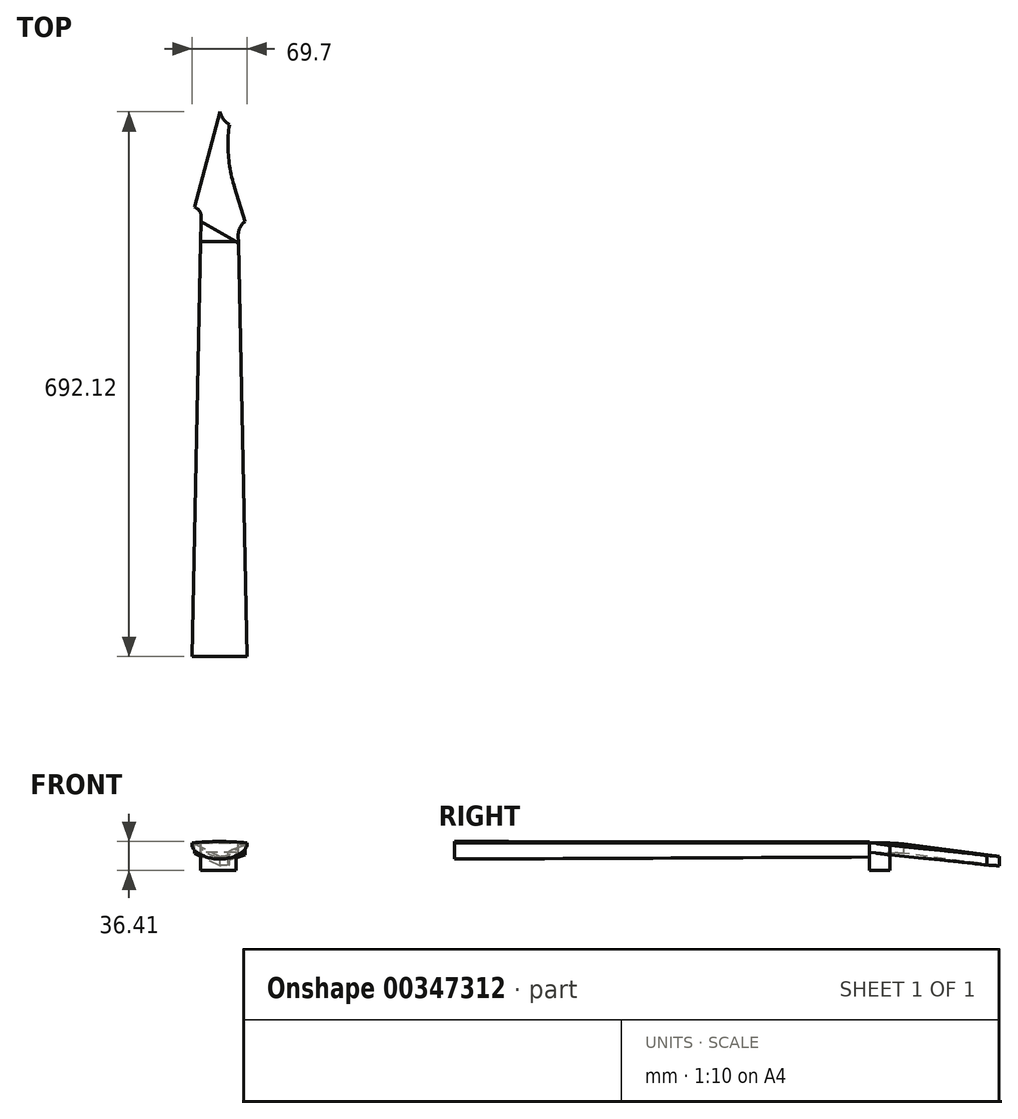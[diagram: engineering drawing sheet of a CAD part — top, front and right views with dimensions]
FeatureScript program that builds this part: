
annotation { "Feature Type Name" : "Feature", "Feature Type Description" : "" }
export const myFeature = defineFeature(function(context is Context, id is Id, definition is map)
    precondition{}
    {
        {
            var Q0;
            Q0=qCreatedBy(makeId("Top.planeOp"),FACE);
            var sketch = newSketch(context, id + "F0", { "sketchPlane" : qUnion([Q0])});
            skLineSegment(sketch, "E0", {"start": v(-24, 485.77) * mm, "end": v(24, 485.77) * mm, "construction": true});
            skLineSegment(sketch, "E1", {"start": v(-50, -161.93) * mm, "end": v(50, -161.93) * mm, "construction": true});
            skLineSegment(sketch, "E2", {"start": v(0, 485.77) * mm, "end": v(0, -161.93) * mm, "construction": true});
            skLineSegment(sketch, "E3", {"start": v(-34, 0) * mm, "end": v(34, 0) * mm, "construction": true});
            skPoint(sketch, "E4", {"position": v(0, 0) * mm});
            skPoint(sketch, "E5", {"position": v(21, 485.77) * mm});
            skSolve(sketch);
        }
        {
            var Q0;
            Q0=qCreatedBy(makeId("Top.planeOp"),FACE);
            var sketch = newSketch(context, id + "F1", { "sketchPlane" : qUnion([Q0])});
            skLineSegment(sketch, "E6", {"start": v(24, 485.77) * mm, "end": v(21, 485.77) * mm, "construction": true});
            skLineSegment(sketch, "E7", {"start": v(21, 485.77) * mm, "end": v(20.77, 485.77) * mm});
            skLineSegment(sketch, "E8", {"start": v(20.77, 485.77) * mm, "end": v(14.57, 485.77) * mm, "construction": true});
            skLineSegment(sketch, "E9", {"start": v(14.57, 485.77) * mm, "end": v(14.29, 485.77) * mm});
            skLineSegment(sketch, "E10", {"start": v(14.29, 485.77) * mm, "end": v(8.08, 485.77) * mm, "construction": true});
            skLineSegment(sketch, "E11", {"start": v(8.08, 485.77) * mm, "end": v(7.68, 485.77) * mm});
            skLineSegment(sketch, "E12", {"start": v(7.68, 485.77) * mm, "end": v(1.47, 485.77) * mm, "construction": true});
            skLineSegment(sketch, "E13", {"start": v(1.47, 485.77) * mm, "end": v(0.86, 485.77) * mm});
            skLineSegment(sketch, "E14", {"start": v(0.86, 485.77) * mm, "end": v(-5.34, 485.77) * mm, "construction": true});
            skLineSegment(sketch, "E15", {"start": v(-5.34, 485.77) * mm, "end": v(-6.15, 485.77) * mm});
            skLineSegment(sketch, "E16", {"start": v(-6.15, 485.77) * mm, "end": v(-12.36, 485.77) * mm, "construction": true});
            skLineSegment(sketch, "E17", {"start": v(-12.36, 485.77) * mm, "end": v(-13.42, 485.77) * mm});
            skLineSegment(sketch, "E18", {"start": v(-13.42, 485.77) * mm, "end": v(-19.63, 485.77) * mm, "construction": true});
            skLineSegment(sketch, "E19", {"start": v(-19.63, 485.77) * mm, "end": v(-21, 485.77) * mm});
            skLineSegment(sketch, "E20", {"start": v(-21, 485.77) * mm, "end": v(-24, 485.77) * mm, "construction": true});
            skPoint(sketch, "E21", {"position": v(-20.32, 485.77) * mm});
            skPoint(sketch, "E22", {"position": v(-12.9, 485.77) * mm});
            skPoint(sketch, "E23", {"position": v(-5.75, 485.77) * mm});
            skPoint(sketch, "E24", {"position": v(1.17, 485.77) * mm});
            skPoint(sketch, "E25", {"position": v(7.88, 485.77) * mm});
            skPoint(sketch, "E26", {"position": v(14.43, 485.77) * mm});
            skPoint(sketch, "E27", {"position": v(20.89, 485.77) * mm});
            skLineSegment(sketch, "E28", {"start": v(34, 0) * mm, "end": v(30.89, 0) * mm});
            skLineSegment(sketch, "E29", {"start": v(30.89, 0) * mm, "end": v(30.66, 0) * mm});
            skLineSegment(sketch, "E30", {"start": v(30.66, 0) * mm, "end": v(21.16, 0) * mm});
            skLineSegment(sketch, "E31", {"start": v(21.16, 0) * mm, "end": v(20.88, 0) * mm});
            skLineSegment(sketch, "E32", {"start": v(20.88, 0) * mm, "end": v(11.38, 0) * mm});
            skLineSegment(sketch, "E33", {"start": v(11.38, 0) * mm, "end": v(10.97, 0) * mm});
            skLineSegment(sketch, "E34", {"start": v(10.97, 0) * mm, "end": v(1.47, 0) * mm});
            skLineSegment(sketch, "E35", {"start": v(1.47, 0) * mm, "end": v(0.86, 0) * mm});
            skLineSegment(sketch, "E36", {"start": v(0.86, 0) * mm, "end": v(-8.64, 0) * mm});
            skLineSegment(sketch, "E37", {"start": v(-8.64, 0) * mm, "end": v(-9.45, 0) * mm});
            skLineSegment(sketch, "E38", {"start": v(-9.45, 0) * mm, "end": v(-18.95, 0) * mm});
            skLineSegment(sketch, "E39", {"start": v(-18.95, 0) * mm, "end": v(-20.02, 0) * mm});
            skLineSegment(sketch, "E40", {"start": v(-20.02, 0) * mm, "end": v(-29.52, 0) * mm});
            skLineSegment(sketch, "E41", {"start": v(-29.52, 0) * mm, "end": v(-30.89, 0) * mm});
            skLineSegment(sketch, "E42", {"start": v(-30.89, 0) * mm, "end": v(-34, 0) * mm});
            skPoint(sketch, "E43", {"position": v(-30.2, 0) * mm});
            skPoint(sketch, "E44", {"position": v(-19.48, 0) * mm});
            skPoint(sketch, "E45", {"position": v(-9.04, 0) * mm});
            skPoint(sketch, "E46", {"position": v(1.17, 0) * mm});
            skPoint(sketch, "E47", {"position": v(11.18, 0) * mm});
            skPoint(sketch, "E48", {"position": v(21.02, 0) * mm});
            skPoint(sketch, "E49", {"position": v(30.78, 0) * mm});
            skLineSegment(sketch, "E50", {"start": v(37.19, -161.93) * mm, "end": v(34.19, -161.93) * mm, "construction": true});
            skLineSegment(sketch, "E51", {"start": v(34.19, -161.93) * mm, "end": v(33.96, -161.93) * mm});
            skLineSegment(sketch, "E52", {"start": v(33.96, -161.93) * mm, "end": v(23.36, -161.93) * mm, "construction": true});
            skLineSegment(sketch, "E53", {"start": v(23.36, -161.93) * mm, "end": v(23.08, -161.93) * mm});
            skLineSegment(sketch, "E54", {"start": v(23.08, -161.93) * mm, "end": v(12.48, -161.93) * mm, "construction": true});
            skLineSegment(sketch, "E55", {"start": v(12.48, -161.93) * mm, "end": v(12.07, -161.93) * mm});
            skLineSegment(sketch, "E56", {"start": v(12.07, -161.93) * mm, "end": v(1.47, -161.93) * mm, "construction": true});
            skLineSegment(sketch, "E57", {"start": v(1.47, -161.93) * mm, "end": v(0.86, -161.93) * mm});
            skLineSegment(sketch, "E58", {"start": v(0.86, -161.93) * mm, "end": v(-9.74, -161.93) * mm, "construction": true});
            skLineSegment(sketch, "E59", {"start": v(-9.74, -161.93) * mm, "end": v(-10.55, -161.93) * mm});
            skLineSegment(sketch, "E60", {"start": v(-10.55, -161.93) * mm, "end": v(-21.15, -161.93) * mm, "construction": true});
            skLineSegment(sketch, "E61", {"start": v(-21.15, -161.93) * mm, "end": v(-22.21, -161.93) * mm});
            skLineSegment(sketch, "E62", {"start": v(-22.21, -161.93) * mm, "end": v(-32.81, -161.93) * mm, "construction": true});
            skLineSegment(sketch, "E63", {"start": v(-32.81, -161.93) * mm, "end": v(-34.19, -161.93) * mm});
            skLineSegment(sketch, "E64", {"start": v(-34.19, -161.93) * mm, "end": v(-37.19, -161.93) * mm, "construction": true});
            skPoint(sketch, "E65", {"position": v(-33.5, -161.93) * mm});
            skPoint(sketch, "E66", {"position": v(-21.68, -161.93) * mm});
            skPoint(sketch, "E67", {"position": v(-10.14, -161.93) * mm});
            skPoint(sketch, "E68", {"position": v(1.17, -161.93) * mm});
            skPoint(sketch, "E69", {"position": v(12.28, -161.93) * mm});
            skPoint(sketch, "E70", {"position": v(23.22, -161.93) * mm});
            skPoint(sketch, "E71", {"position": v(34.07, -161.93) * mm});
            skLineSegment(sketch, "E72", {"start": v(-37.19, -161.93) * mm, "end": v(-37.19, -211.93) * mm, "construction": true});
            skLineSegment(sketch, "E73", {"start": v(-37.19, -211.93) * mm, "end": v(37.19, -211.93) * mm, "construction": true});
            skLineSegment(sketch, "E74", {"start": v(37.19, -211.93) * mm, "end": v(37.19, -161.93) * mm, "construction": true});
            skPoint(sketch, "E75", {"position": v(0, -211.93) * mm});
            skLineSegment(sketch, "E76", {"start": v(-24, 485.77) * mm, "end": v(-23.38, 515.77) * mm, "construction": true});
            skLineSegment(sketch, "E77", {"start": v(-23.38, 515.77) * mm, "end": v(23.38, 515.77) * mm, "construction": true});
            skLineSegment(sketch, "E78", {"start": v(23.38, 515.77) * mm, "end": v(24, 485.77) * mm, "construction": true});
            skLineSegment(sketch, "E79", {"start": v(24, 485.77) * mm, "end": v(38.36, -211.93) * mm});
            skLineSegment(sketch, "E80", {"start": v(-24, 485.78) * mm, "end": v(-38.36, -211.93) * mm});
            skSolve(sketch);
        }
        {
            var Q0;
            Q0=qCreatedBy(makeId("Top.planeOp"),FACE);
            var sketch = newSketch(context, id + "F2", { "sketchPlane" : qUnion([Q0])});
            skLineSegment(sketch, "E81", {"start": v(17.82, 636.3) * mm, "end": v(34.14, -165.06) * mm});
            skLineSegment(sketch, "E82", {"start": v(-17.25, 636.37) * mm, "end": v(-34.31, -201.78) * mm});
            skSolve(sketch);
        }
        {
            var Q0;
            Q0=qCreatedBy(makeId("Top.planeOp"),FACE);
            var sketch = newSketch(context, id + "F3", { "sketchPlane" : qUnion([Q0])});
            skLineSegment(sketch, "E83", {"start": v(23.32, -169.15) * mm, "end": v(12.4, 634.88) * mm});
            skLineSegment(sketch, "E84", {"start": v(-10.88, 634.32) * mm, "end": v(-22.08, -191.54) * mm});
            skLineSegment(sketch, "E85", {"start": v(12.36, -173.72) * mm, "end": v(6.89, 632.04) * mm});
            skLineSegment(sketch, "E86", {"start": v(-10.3, -185.7) * mm, "end": v(-4.74, 634.55) * mm});
            skLineSegment(sketch, "E87", {"start": v(1.17, 632.04) * mm, "end": v(1.17, -180.14) * mm});
            skSolve(sketch);
        }
        {
            var Q0;
            Q0=qCreatedBy(makeId("Top.planeOp"),FACE);
            var sketch = newSketch(context, id + "F4", { "sketchPlane" : qUnion([Q0])});
            skLineSegment(sketch, "E88", {"start": v(0, 515.7) * mm, "end": v(0, -207.7) * mm});
            skLineSegment(sketch, "E89", {"start": v(-52.5, 223.2) * mm, "end": v(52.5, 223.2) * mm});
            skPoint(sketch, "E90", {"position": v(0, 223.2) * mm});
            skLineSegment(sketch, "E91", {"start": v(0, 246.1) * mm, "end": v(52.5, 246.1) * mm});
            skLineSegment(sketch, "E92", {"start": v(52.5, 270.36) * mm, "end": v(0, 270.36) * mm});
            skLineSegment(sketch, "E93", {"start": v(0, 323.3) * mm, "end": v(52.5, 323.3) * mm});
            skLineSegment(sketch, "E94", {"start": v(52.5, 352.15) * mm, "end": v(0, 352.15) * mm});
            skLineSegment(sketch, "E95", {"start": v(0, 382.72) * mm, "end": v(52.5, 382.72) * mm});
            skLineSegment(sketch, "E96", {"start": v(52.5, 415.1) * mm, "end": v(0, 415.1) * mm});
            skLineSegment(sketch, "E97", {"start": v(0, 449.42) * mm, "end": v(52.5, 449.42) * mm});
            skLineSegment(sketch, "E98", {"start": v(52.5, 485.77) * mm, "end": v(0, 485.77) * mm});
            skLineSegment(sketch, "E99", {"start": v(0, 432.42) * mm, "end": v(-52.5, 432.42) * mm});
            skLineSegment(sketch, "E100", {"start": v(0, 397.11) * mm, "end": v(-52.5, 397.11) * mm});
            skLineSegment(sketch, "E101", {"start": v(-52.5, 363.79) * mm, "end": v(0, 363.79) * mm});
            skLineSegment(sketch, "E102", {"start": v(0, 469.83) * mm, "end": v(-52.5, 469.83) * mm});
            skLineSegment(sketch, "E103", {"start": v(-52.5, 332.33) * mm, "end": v(0, 332.33) * mm});
            skLineSegment(sketch, "E104", {"start": v(0, 302.64) * mm, "end": v(-52.5, 302.64) * mm});
            skLineSegment(sketch, "E105", {"start": v(-52.5, 274.62) * mm, "end": v(0, 274.62) * mm});
            skLineSegment(sketch, "E106", {"start": v(0, 80.69) * mm, "end": v(52.5, 80.69) * mm});
            skLineSegment(sketch, "E107", {"start": v(52.5, 95.12) * mm, "end": v(0, 95.12) * mm});
            skLineSegment(sketch, "E108", {"start": v(0, 110.4) * mm, "end": v(52.5, 110.4) * mm});
            skLineSegment(sketch, "E109", {"start": v(52.5, 126.6) * mm, "end": v(0, 126.6) * mm});
            skLineSegment(sketch, "E110", {"start": v(0, 143.75) * mm, "end": v(52.5, 143.75) * mm});
            skLineSegment(sketch, "E111", {"start": v(52.5, 161.93) * mm, "end": v(0, 161.93) * mm});
            skLineSegment(sketch, "E112", {"start": v(0, 181.18) * mm, "end": v(52.5, 181.18) * mm});
            skLineSegment(sketch, "E113", {"start": v(52.5, 201.58) * mm, "end": v(0, 201.58) * mm});
            skLineSegment(sketch, "E114", {"start": v(-52.5, 83.56) * mm, "end": v(0, 83.56) * mm});
            skLineSegment(sketch, "E115", {"start": v(0, 100.22) * mm, "end": v(-52.5, 100.22) * mm});
            skLineSegment(sketch, "E116", {"start": v(-52.5, 117.88) * mm, "end": v(0, 117.88) * mm});
            skLineSegment(sketch, "E117", {"start": v(0, 136.58) * mm, "end": v(-52.5, 136.58) * mm});
            skLineSegment(sketch, "E118", {"start": v(-52.5, 156.4) * mm, "end": v(0, 156.4) * mm});
            skLineSegment(sketch, "E119", {"start": v(0, 177.4) * mm, "end": v(-52.5, 177.4) * mm});
            skLineSegment(sketch, "E120", {"start": v(-52.5, 199.63) * mm, "end": v(0, 199.63) * mm});
            skLineSegment(sketch, "E121", {"start": v(0, 248.17) * mm, "end": v(-52.5, 248.17) * mm});
            skLineSegment(sketch, "E122", {"start": v(0, 296.07) * mm, "end": v(52.5, 296.07) * mm});
            skLineSegment(sketch, "E123", {"start": v(0, 0) * mm, "end": v(52.5, 0) * mm});
            skLineSegment(sketch, "E124", {"start": v(52.5, 9.63) * mm, "end": v(0, 9.63) * mm});
            skLineSegment(sketch, "E125", {"start": v(0, 19.83) * mm, "end": v(52.5, 19.83) * mm});
            skLineSegment(sketch, "E126", {"start": v(52.5, 30.64) * mm, "end": v(0, 30.64) * mm});
            skLineSegment(sketch, "E127", {"start": v(0, 42.09) * mm, "end": v(52.5, 42.09) * mm});
            skLineSegment(sketch, "E128", {"start": v(52.5, 54.22) * mm, "end": v(0, 54.22) * mm});
            skLineSegment(sketch, "E129", {"start": v(0, 67.07) * mm, "end": v(52.5, 67.07) * mm});
            skLineSegment(sketch, "E130", {"start": v(0, -161.93) * mm, "end": v(52.5, -161.93) * mm});
            skLineSegment(sketch, "E131", {"start": v(0, -196.66) * mm, "end": v(-52.5, -196.66) * mm});
            skLineSegment(sketch, "E132", {"start": v(0, 509.46) * mm, "end": v(-60, 509.46) * mm});
            skLineSegment(sketch, "E133", {"start": v(-52.5, -9.64) * mm, "end": v(0, -9.64) * mm});
            skLineSegment(sketch, "E134", {"start": v(0, 1.49) * mm, "end": v(-52.5, 1.49) * mm});
            skLineSegment(sketch, "E135", {"start": v(-52.5, 13.27) * mm, "end": v(0, 13.27) * mm});
            skLineSegment(sketch, "E136", {"start": v(0, 25.75) * mm, "end": v(-52.5, 25.75) * mm});
            skLineSegment(sketch, "E137", {"start": v(-52.5, 38.98) * mm, "end": v(0, 38.98) * mm});
            skLineSegment(sketch, "E138", {"start": v(0, 52.99) * mm, "end": v(-52.5, 52.99) * mm});
            skLineSegment(sketch, "E139", {"start": v(-52.5, 67.83) * mm, "end": v(0, 67.83) * mm});
            skLineSegment(sketch, "E140", {"start": v(0, -20.13) * mm, "end": v(-52.5, -20.13) * mm});
            skSolve(sketch);
        }
        {
            var Q0;
            Q0=qCreatedBy(makeId("Top.planeOp"),FACE);
            var sketch = newSketch(context, id + "F5", { "sketchPlane" : qUnion([Q0])});
            skLineSegment(sketch, "E141", {"start": v(24.04, 483.94) * mm, "end": v(-23.47, 511.57) * mm});
            skPoint(sketch, "E142", {"position": v(-19.83, 509.46) * mm});
            skLineSegment(sketch, "E143", {"start": v(-24.3, 471.6) * mm, "end": v(24.78, 447.9) * mm});
            skLineSegment(sketch, "E144", {"start": v(-25.07, 433.87) * mm, "end": v(25.48, 413.86) * mm});
            skLineSegment(sketch, "E145", {"start": v(-25.8, 398.29) * mm, "end": v(26.14, 381.72) * mm});
            skLineSegment(sketch, "E146", {"start": v(-26.5, 364.71) * mm, "end": v(26.77, 351.36) * mm});
            skLineSegment(sketch, "E147", {"start": v(-27.14, 333.03) * mm, "end": v(27.36, 322.7) * mm});
            skLineSegment(sketch, "E148", {"start": v(-27.76, 303.14) * mm, "end": v(27.91, 295.64) * mm});
            skLineSegment(sketch, "E149", {"start": v(-28.34, 274.93) * mm, "end": v(28.44, 270.1) * mm});
            skLineSegment(sketch, "E150", {"start": v(-28.89, 248.32) * mm, "end": v(28.94, 245.97) * mm});
            skLineSegment(sketch, "E151", {"start": v(-29.4, 223.2) * mm, "end": v(29.4, 223.2) * mm});
            skLineSegment(sketch, "E152", {"start": v(29.85, 201.7) * mm, "end": v(-29.9, 199.5) * mm});
            skLineSegment(sketch, "E153", {"start": v(30.27, 181.4) * mm, "end": v(-30.35, 177.13) * mm});
            skLineSegment(sketch, "E154", {"start": v(30.66, 162.25) * mm, "end": v(-30.79, 156.02) * mm});
            skLineSegment(sketch, "E155", {"start": v(31.03, 144.16) * mm, "end": v(-31.2, 136.1) * mm});
            skLineSegment(sketch, "E156", {"start": v(31.38, 127.09) * mm, "end": v(-31.59, 117.3) * mm});
            skLineSegment(sketch, "E157", {"start": v(32.03, 95.76) * mm, "end": v(-32.3, 82.8) * mm});
            skLineSegment(sketch, "E158", {"start": v(32.32, 81.4) * mm, "end": v(-32.62, 67) * mm});
            skLineSegment(sketch, "E159", {"start": v(32.6, 67.84) * mm, "end": v(-32.93, 52.07) * mm});
            skLineSegment(sketch, "E160", {"start": v(32.87, 55.04) * mm, "end": v(-33.22, 38) * mm});
            skLineSegment(sketch, "E161", {"start": v(33.12, 42.97) * mm, "end": v(-33.5, 24.7) * mm});
            skLineSegment(sketch, "E162", {"start": v(33.35, 31.56) * mm, "end": v(-33.75, 12.17) * mm});
            skLineSegment(sketch, "E163", {"start": v(33.57, 20.8) * mm, "end": v(-34, 0.33) * mm});
            skLineSegment(sketch, "E164", {"start": v(33.78, 10.64) * mm, "end": v(-34.22, -10.84) * mm});
            skLineSegment(sketch, "E165", {"start": v(33.98, 1.05) * mm, "end": v(-34.44, -21.39) * mm});
            skPoint(sketch, "E166", {"position": v(-30.61, -20.13) * mm});
            skPoint(sketch, "E167", {"position": v(-30.4, -9.64) * mm});
            skPoint(sketch, "E168", {"position": v(-30.17, 1.49) * mm});
            skPoint(sketch, "E169", {"position": v(-29.93, 13.27) * mm});
            skPoint(sketch, "E170", {"position": v(-29.68, 25.75) * mm});
            skPoint(sketch, "E171", {"position": v(-29.41, 38.98) * mm});
            skPoint(sketch, "E172", {"position": v(-29.13, 52.99) * mm});
            skPoint(sketch, "E173", {"position": v(-28.82, 67.83) * mm});
            skPoint(sketch, "E174", {"position": v(-28.5, 83.56) * mm});
            skPoint(sketch, "E175", {"position": v(-28.16, 100.22) * mm});
            skPoint(sketch, "E176", {"position": v(-27.8, 117.88) * mm});
            skPoint(sketch, "E177", {"position": v(-27.42, 136.58) * mm});
            skPoint(sketch, "E178", {"position": v(-27.02, 156.4) * mm});
            skPoint(sketch, "E179", {"position": v(-26.6, 177.4) * mm});
            skPoint(sketch, "E180", {"position": v(-26.14, 199.63) * mm});
            skPoint(sketch, "E181", {"position": v(-25.66, 223.2) * mm});
            skPoint(sketch, "E182", {"position": v(-25.15, 248.17) * mm});
            skPoint(sketch, "E183", {"position": v(-24.61, 274.62) * mm});
            skPoint(sketch, "E184", {"position": v(-24.04, 302.64) * mm});
            skPoint(sketch, "E185", {"position": v(-23.44, 332.33) * mm});
            skPoint(sketch, "E186", {"position": v(-22.8, 363.79) * mm});
            skPoint(sketch, "E187", {"position": v(-22.12, 397.11) * mm});
            skPoint(sketch, "E188", {"position": v(-21.4, 432.42) * mm});
            skPoint(sketch, "E189", {"position": v(-20.64, 469.83) * mm});
            skLineSegment(sketch, "E190", {"start": v(-31.95, 99.55) * mm, "end": v(31.72, 110.97) * mm});
            skPoint(sketch, "E191", {"position": v(30.58, 9.63) * mm});
            skPoint(sketch, "E192", {"position": v(30.37, 19.83) * mm});
            skPoint(sketch, "E193", {"position": v(30.15, 30.64) * mm});
            skPoint(sketch, "E194", {"position": v(29.92, 42.09) * mm});
            skPoint(sketch, "E195", {"position": v(29.67, 54.22) * mm});
            skPoint(sketch, "E196", {"position": v(29.4, 67.07) * mm});
            skPoint(sketch, "E197", {"position": v(29.13, 80.69) * mm});
            skPoint(sketch, "E198", {"position": v(28.84, 95.12) * mm});
            skPoint(sketch, "E199", {"position": v(28.53, 110.4) * mm});
            skPoint(sketch, "E200", {"position": v(28.2, 126.6) * mm});
            skPoint(sketch, "E201", {"position": v(27.85, 143.75) * mm});
            skPoint(sketch, "E202", {"position": v(27.48, 161.93) * mm});
            skPoint(sketch, "E203", {"position": v(27.09, 181.18) * mm});
            skPoint(sketch, "E204", {"position": v(26.67, 201.58) * mm});
            skPoint(sketch, "E205", {"position": v(26.23, 223.2) * mm});
            skPoint(sketch, "E206", {"position": v(25.77, 246.1) * mm});
            skPoint(sketch, "E207", {"position": v(25.27, 270.36) * mm});
            skPoint(sketch, "E208", {"position": v(24.75, 296.07) * mm});
            skPoint(sketch, "E209", {"position": v(24.2, 323.3) * mm});
            skPoint(sketch, "E210", {"position": v(23.6, 352.15) * mm});
            skPoint(sketch, "E211", {"position": v(22.98, 382.72) * mm});
            skPoint(sketch, "E212", {"position": v(22.33, 415.1) * mm});
            skPoint(sketch, "E213", {"position": v(21.63, 449.42) * mm});
            skLineSegment(sketch, "E214", {"start": v(34.07, -161.92) * mm, "end": v(-34.2, -196.66) * mm});
            skSolve(sketch);
        }
        {
            var Q0;
            Q0=qCreatedBy(makeId("Top.planeOp"),FACE);
            var sketch = newSketch(context, id + "F6", { "sketchPlane" : qUnion([Q0])});
            skCircle(sketch, "E215", {"center": v(-28.12, 544.63) * mm, "radius": 3 * mm});
            skCircle(sketch, "E216", {"center": v(20.37, 536.39) * mm, "radius": 3 * mm});
            skCircle(sketch, "E217", {"center": v(28.47, 515.94) * mm, "radius": 3 * mm});
            skLineSegment(sketch, "E218", {"start": v(-28.12, 544.63) * mm, "end": v(-19.36, 564.81) * mm, "construction": true});
            skCircle(sketch, "E219", {"center": v(-28.12, 544.63) * mm, "radius": 8.15 * mm, "construction": true});
            skCircle(sketch, "E220", {"center": v(-19.36, 564.81) * mm, "radius": 8.15 * mm, "construction": true});
            skCircle(sketch, "E221", {"center": v(-10.6, 585) * mm, "radius": 8.15 * mm, "construction": true});
            skCircle(sketch, "E222", {"center": v(28.47, 515.94) * mm, "radius": 8.15 * mm, "construction": true});
            skLineSegment(sketch, "E223", {"start": v(-23.47, 511.57) * mm, "end": v(-25.07, 433.87) * mm});
            skLineSegment(sketch, "E224", {"start": v(24.04, 483.94) * mm, "end": v(25.48, 413.86) * mm});
            skLineSegment(sketch, "E225", {"start": v(-19.36, 564.81) * mm, "end": v(-10.6, 585) * mm, "construction": true});
            skCircle(sketch, "E226", {"center": v(-1.83, 605.17) * mm, "radius": 3 * mm});
            skCircle(sketch, "E227", {"center": v(-1.83, 605.17) * mm, "radius": 8.15 * mm, "construction": true});
            skLineSegment(sketch, "E228", {"start": v(-10.6, 585) * mm, "end": v(-1.83, 605.17) * mm, "construction": true});
            skLineSegment(sketch, "E229", {"start": v(12.27, 556.84) * mm, "end": v(20.37, 536.39) * mm, "construction": true});
            skLineSegment(sketch, "E230", {"start": v(20.37, 536.39) * mm, "end": v(28.47, 515.94) * mm, "construction": true});
            skLineSegment(sketch, "E231", {"start": v(-38.84, 540.4) * mm, "end": v(6.93, 645.82) * mm});
            skCircle(sketch, "E232", {"center": v(6.93, 625.35) * mm, "radius": 3 * mm});
            skCircle(sketch, "E233", {"center": v(6.93, 625.35) * mm, "radius": 8.15 * mm, "construction": true});
            skLineSegment(sketch, "E234", {"start": v(6.93, 625.35) * mm, "end": v(-1.83, 605.17) * mm, "construction": true});
            skLineSegment(sketch, "E235", {"start": v(12.27, 556.84) * mm, "end": v(4.17, 577.3) * mm, "construction": true});
            skCircle(sketch, "E236", {"center": v(4.17, 577.3) * mm, "radius": 3 * mm, "construction": true});
            skLineSegment(sketch, "E237", {"start": v(-28.12, 544.63) * mm, "end": v(-19.12, 544.45) * mm, "construction": true});
            skLineSegment(sketch, "E238", {"start": v(28.47, 515.94) * mm, "end": v(20.28, 515.77) * mm, "construction": true});
            skPoint(sketch, "E239", {"position": v(20.89, 485.77) * mm});
            skLineSegment(sketch, "E240", {"start": v(35.32, 520.36) * mm, "end": v(39.74, 513.52) * mm});
            skLineSegment(sketch, "E241", {"start": v(39.74, 513.52) * mm, "end": v(32.9, 509.1) * mm, "construction": true});
            skArc(sketch, "E242", {"start": v(24.04, 483.94) * mm, "mid": v(28.05, 500.77) * mm, "end": v(39.74, 513.52) * mm});
            skLineSegment(sketch, "E243", {"start": v(-38.84, 540.4) * mm, "end": v(-31.36, 537.16) * mm, "construction": true});
            skLineSegment(sketch, "E244", {"start": v(-23.47, 511.57) * mm, "end": v(-23.37, 516.29) * mm});
            skArc(sketch, "E245", {"start": v(-23.37, 516.29) * mm, "mid": v(-27.44, 530.7) * mm, "end": v(-38.84, 540.4) * mm});
            skArc(sketch, "E246", {"start": v(6.93, 645.82) * mm, "mid": v(9.7, 635.66) * mm, "end": v(16.41, 627.54) * mm});
            skArc(sketch, "E247", {"start": v(35.32, 520.36) * mm, "mid": v(15.02, 572.04) * mm, "end": v(16.41, 627.54) * mm});
            skCircle(sketch, "E248", {"center": v(-10.6, 585) * mm, "radius": 3 * mm});
            skCircle(sketch, "E249", {"center": v(-19.36, 564.81) * mm, "radius": 3 * mm});
            skLineSegment(sketch, "E250", {"start": v(6.93, 625.35) * mm, "end": v(-0.55, 628.6) * mm, "construction": true});
            skSolve(sketch);
        }
        {
            var Q0;
            Q0=qCreatedBy(makeId("Top.planeOp"),FACE);
            var sketch = newSketch(context, id + "F7", { "sketchPlane" : qUnion([Q0])});
            skCircle(sketch, "E251", {"center": v(-22.34, 533.57) * mm, "radius": 3 * mm});
            skCircle(sketch, "E252", {"center": v(-22.34, 533.57) * mm, "radius": 8.15 * mm, "construction": true});
            skCircle(sketch, "E253", {"center": v(-14.87, 561.3) * mm, "radius": 3 * mm});
            skCircle(sketch, "E254", {"center": v(-14.87, 561.3) * mm, "radius": 8.15 * mm, "construction": true});
            skCircle(sketch, "E255", {"center": v(-8.06, 586.53) * mm, "radius": 3 * mm});
            skCircle(sketch, "E256", {"center": v(-8.06, 586.53) * mm, "radius": 8.15 * mm, "construction": true});
            skCircle(sketch, "E257", {"center": v(-1.83, 609.64) * mm, "radius": 3 * mm});
            skCircle(sketch, "E258", {"center": v(-1.83, 609.64) * mm, "radius": 8.15 * mm, "construction": true});
            skCircle(sketch, "E259", {"center": v(3.9, 630.88) * mm, "radius": 3 * mm});
            skCircle(sketch, "E260", {"center": v(3.9, 630.88) * mm, "radius": 8.15 * mm, "construction": true});
            skLineSegment(sketch, "E261", {"start": v(3.9, 630.88) * mm, "end": v(-1.83, 609.64) * mm, "construction": true});
            skLineSegment(sketch, "E262", {"start": v(-1.83, 609.64) * mm, "end": v(-8.06, 586.53) * mm, "construction": true});
            skLineSegment(sketch, "E263", {"start": v(-8.06, 586.53) * mm, "end": v(-14.87, 561.3) * mm, "construction": true});
            skLineSegment(sketch, "E264", {"start": v(-14.87, 561.3) * mm, "end": v(-22.34, 533.57) * mm, "construction": true});
            skCircle(sketch, "E265", {"center": v(23.31, 514.04) * mm, "radius": 3 * mm});
            skCircle(sketch, "E266", {"center": v(23.31, 514.04) * mm, "radius": 8.15 * mm, "construction": true});
            skCircle(sketch, "E267", {"center": v(16.76, 535.04) * mm, "radius": 3 * mm});
            skCircle(sketch, "E268", {"center": v(16.76, 535.04) * mm, "radius": 8.15 * mm, "construction": true});
            skLineSegment(sketch, "E269", {"start": v(16.76, 535.04) * mm, "end": v(23.31, 514.04) * mm, "construction": true});
            skLineSegment(sketch, "E270", {"start": v(-25.07, 433.87) * mm, "end": v(-23.47, 511.57) * mm});
            skLineSegment(sketch, "E271", {"start": v(25.48, 413.86) * mm, "end": v(24.04, 483.94) * mm});
            skLineSegment(sketch, "E272", {"start": v(-31.86, 529.57) * mm, "end": v(0.84, 650.86) * mm});
            skLineSegment(sketch, "E273", {"start": v(-23.47, 511.57) * mm, "end": v(-23.34, 518.07) * mm});
            skArc(sketch, "E274", {"start": v(-23.34, 518.07) * mm, "mid": v(-25.63, 525.28) * mm, "end": v(-31.86, 529.57) * mm});
            skLineSegment(sketch, "E275", {"start": v(24.04, 483.94) * mm, "end": v(23.83, 493.94) * mm});
            skLineSegment(sketch, "E276", {"start": v(32.65, 511.48) * mm, "end": v(19.25, 554.4) * mm});
            skArc(sketch, "E277", {"start": v(23.83, 493.94) * mm, "mid": v(26.06, 503.8) * mm, "end": v(32.65, 511.48) * mm});
            skArc(sketch, "E278", {"start": v(0.84, 650.86) * mm, "mid": v(5.02, 641.55) * mm, "end": v(12.58, 634.68) * mm});
            skLineSegment(sketch, "E279", {"start": v(-23.47, 511.57) * mm, "end": v(1.17, 511.57) * mm});
            skLineSegment(sketch, "E280", {"start": v(3.9, 630.88) * mm, "end": v(-3.97, 633) * mm, "construction": true});
            skArc(sketch, "E281", {"start": v(12.58, 634.68) * mm, "mid": v(11.5, 594.18) * mm, "end": v(19.25, 554.4) * mm});
            skSolve(sketch);
        }
        {
            var Q0;
            Q0=qCreatedBy(makeId("Top.planeOp"),FACE);
            var sketch = newSketch(context, id + "F8", { "sketchPlane" : qUnion([Q0])});
            skLineSegment(sketch, "E282.0", {"start": v(17.82, 636.3) * mm, "end": v(30.78, 0) * mm});
            skLineSegment(sketch, "E282.1", {"start": v(-17.25, 636.37) * mm, "end": v(-34.31, -201.78) * mm});
            skLineSegment(sketch, "E282.2", {"start": v(-17.25, 636.37) * mm, "end": v(-30.61, -20.13) * mm});
            skLineSegment(sketch, "E283.0", {"start": v(23.32, -169.15) * mm, "end": v(12.4, 634.88) * mm});
            skLineSegment(sketch, "E283.1", {"start": v(-10.88, 634.32) * mm, "end": v(-22.08, -191.54) * mm});
            skLineSegment(sketch, "E283.2", {"start": v(12.36, -173.72) * mm, "end": v(6.89, 632.04) * mm});
            skLineSegment(sketch, "E283.3", {"start": v(-10.3, -185.7) * mm, "end": v(-4.74, 634.55) * mm});
            skLineSegment(sketch, "E283.4", {"start": v(1.17, 632.04) * mm, "end": v(1.17, -180.14) * mm});
            skLineSegment(sketch, "E283.5", {"start": v(-10.3, -185.7) * mm, "end": v(-4.74, 634.55) * mm});
            skLineSegment(sketch, "E284.0", {"start": v(24.04, 483.94) * mm, "end": v(-23.47, 511.57) * mm});
            skPoint(sketch, "E284.1", {"position": v(-19.83, 509.46) * mm});
            skLineSegment(sketch, "E284.2", {"start": v(-24.3, 471.6) * mm, "end": v(24.78, 447.9) * mm});
            skLineSegment(sketch, "E284.3", {"start": v(-25.07, 433.87) * mm, "end": v(25.48, 413.86) * mm});
            skLineSegment(sketch, "E284.4", {"start": v(-25.8, 398.29) * mm, "end": v(26.14, 381.72) * mm});
            skLineSegment(sketch, "E284.5", {"start": v(-26.5, 364.71) * mm, "end": v(26.77, 351.36) * mm});
            skLineSegment(sketch, "E284.6", {"start": v(-27.14, 333.03) * mm, "end": v(27.36, 322.7) * mm});
            skLineSegment(sketch, "E284.7", {"start": v(-27.76, 303.14) * mm, "end": v(27.91, 295.64) * mm});
            skLineSegment(sketch, "E284.8", {"start": v(-28.34, 274.93) * mm, "end": v(28.44, 270.1) * mm});
            skLineSegment(sketch, "E284.9", {"start": v(-28.89, 248.32) * mm, "end": v(28.94, 245.97) * mm});
            skLineSegment(sketch, "E284.10", {"start": v(-29.4, 223.2) * mm, "end": v(29.4, 223.2) * mm});
            skLineSegment(sketch, "E284.11", {"start": v(29.85, 201.7) * mm, "end": v(-29.9, 199.5) * mm});
            skLineSegment(sketch, "E284.12", {"start": v(30.27, 181.4) * mm, "end": v(-30.35, 177.13) * mm});
            skLineSegment(sketch, "E284.13", {"start": v(30.66, 162.25) * mm, "end": v(-30.79, 156.02) * mm});
            skLineSegment(sketch, "E284.14", {"start": v(31.03, 144.16) * mm, "end": v(-31.2, 136.1) * mm});
            skLineSegment(sketch, "E284.15", {"start": v(31.38, 127.09) * mm, "end": v(-31.59, 117.3) * mm});
            skLineSegment(sketch, "E284.16", {"start": v(32.03, 95.76) * mm, "end": v(-32.3, 82.8) * mm});
            skLineSegment(sketch, "E284.17", {"start": v(32.32, 81.4) * mm, "end": v(-32.62, 67) * mm});
            skLineSegment(sketch, "E284.18", {"start": v(32.6, 67.84) * mm, "end": v(-32.93, 52.07) * mm});
            skLineSegment(sketch, "E284.19", {"start": v(32.87, 55.04) * mm, "end": v(-33.22, 38) * mm});
            skLineSegment(sketch, "E284.20", {"start": v(33.12, 42.97) * mm, "end": v(-33.5, 24.7) * mm});
            skLineSegment(sketch, "E284.21", {"start": v(33.35, 31.56) * mm, "end": v(-33.75, 12.17) * mm});
            skLineSegment(sketch, "E284.22", {"start": v(33.57, 20.8) * mm, "end": v(-34, 0.33) * mm});
            skLineSegment(sketch, "E284.23", {"start": v(33.78, 10.64) * mm, "end": v(-34.22, -10.84) * mm});
            skLineSegment(sketch, "E284.24", {"start": v(33.98, 1.05) * mm, "end": v(-34.44, -21.39) * mm});
            skPoint(sketch, "E284.27", {"position": v(-30.17, 1.49) * mm});
            skPoint(sketch, "E284.28", {"position": v(-29.93, 13.27) * mm});
            skPoint(sketch, "E284.29", {"position": v(-29.68, 25.75) * mm});
            skPoint(sketch, "E284.30", {"position": v(-29.41, 38.98) * mm});
            skPoint(sketch, "E284.31", {"position": v(-29.13, 52.99) * mm});
            skPoint(sketch, "E284.32", {"position": v(-28.82, 67.83) * mm});
            skPoint(sketch, "E284.33", {"position": v(-28.5, 83.56) * mm});
            skPoint(sketch, "E284.34", {"position": v(-28.16, 100.22) * mm});
            skPoint(sketch, "E284.35", {"position": v(-27.8, 117.88) * mm});
            skPoint(sketch, "E284.36", {"position": v(-27.42, 136.58) * mm});
            skPoint(sketch, "E284.37", {"position": v(-27.02, 156.4) * mm});
            skPoint(sketch, "E284.38", {"position": v(-26.6, 177.4) * mm});
            skPoint(sketch, "E284.39", {"position": v(-26.14, 199.63) * mm});
            skPoint(sketch, "E284.40", {"position": v(-25.66, 223.2) * mm});
            skPoint(sketch, "E284.41", {"position": v(-25.15, 248.17) * mm});
            skPoint(sketch, "E284.42", {"position": v(-24.61, 274.62) * mm});
            skPoint(sketch, "E284.43", {"position": v(-24.04, 302.64) * mm});
            skPoint(sketch, "E284.44", {"position": v(-23.44, 332.33) * mm});
            skPoint(sketch, "E284.45", {"position": v(-22.8, 363.79) * mm});
            skPoint(sketch, "E284.46", {"position": v(-22.12, 397.11) * mm});
            skPoint(sketch, "E284.47", {"position": v(-21.4, 432.42) * mm});
            skPoint(sketch, "E284.48", {"position": v(-20.64, 469.83) * mm});
            skLineSegment(sketch, "E284.49", {"start": v(-31.95, 99.55) * mm, "end": v(31.72, 110.97) * mm});
            skPoint(sketch, "E284.50", {"position": v(30.58, 9.63) * mm});
            skPoint(sketch, "E284.51", {"position": v(30.37, 19.83) * mm});
            skPoint(sketch, "E284.52", {"position": v(30.15, 30.64) * mm});
            skPoint(sketch, "E284.53", {"position": v(29.92, 42.09) * mm});
            skPoint(sketch, "E284.54", {"position": v(29.67, 54.22) * mm});
            skPoint(sketch, "E284.55", {"position": v(29.4, 67.07) * mm});
            skPoint(sketch, "E284.56", {"position": v(29.13, 80.69) * mm});
            skPoint(sketch, "E284.57", {"position": v(28.84, 95.12) * mm});
            skPoint(sketch, "E284.58", {"position": v(28.53, 110.4) * mm});
            skPoint(sketch, "E284.59", {"position": v(28.2, 126.6) * mm});
            skPoint(sketch, "E284.60", {"position": v(27.85, 143.75) * mm});
            skPoint(sketch, "E284.61", {"position": v(27.48, 161.93) * mm});
            skPoint(sketch, "E284.62", {"position": v(27.09, 181.18) * mm});
            skPoint(sketch, "E284.63", {"position": v(26.67, 201.58) * mm});
            skPoint(sketch, "E284.64", {"position": v(26.23, 223.2) * mm});
            skPoint(sketch, "E284.65", {"position": v(25.77, 246.1) * mm});
            skPoint(sketch, "E284.66", {"position": v(25.27, 270.36) * mm});
            skPoint(sketch, "E284.67", {"position": v(24.75, 296.07) * mm});
            skPoint(sketch, "E284.68", {"position": v(24.2, 323.3) * mm});
            skPoint(sketch, "E284.69", {"position": v(23.6, 352.15) * mm});
            skPoint(sketch, "E284.70", {"position": v(22.98, 382.72) * mm});
            skPoint(sketch, "E284.71", {"position": v(22.33, 415.1) * mm});
            skPoint(sketch, "E284.72", {"position": v(21.63, 449.42) * mm});
            skLineSegment(sketch, "E284.73", {"start": v(34.07, -161.92) * mm, "end": v(-34.2, -196.66) * mm});
            skLineSegment(sketch, "E284.74", {"start": v(33.98, 1.05) * mm, "end": v(-34.44, -21.39) * mm});
            skCircle(sketch, "E285.0", {"center": v(-22.34, 533.57) * mm, "radius": 3 * mm});
            skCircle(sketch, "E285.1", {"center": v(-22.34, 533.57) * mm, "radius": 8.15 * mm});
            skCircle(sketch, "E285.2", {"center": v(-14.87, 561.3) * mm, "radius": 3 * mm});
            skCircle(sketch, "E285.3", {"center": v(-14.87, 561.3) * mm, "radius": 8.15 * mm});
            skCircle(sketch, "E285.4", {"center": v(-8.06, 586.53) * mm, "radius": 3 * mm});
            skCircle(sketch, "E285.5", {"center": v(-8.06, 586.53) * mm, "radius": 8.15 * mm});
            skCircle(sketch, "E285.6", {"center": v(-1.83, 609.64) * mm, "radius": 3 * mm});
            skCircle(sketch, "E285.7", {"center": v(-1.83, 609.64) * mm, "radius": 8.15 * mm});
            skCircle(sketch, "E285.8", {"center": v(3.9, 630.88) * mm, "radius": 3 * mm});
            skCircle(sketch, "E285.9", {"center": v(3.9, 630.88) * mm, "radius": 8.15 * mm});
            skLineSegment(sketch, "E285.10", {"start": v(3.9, 630.88) * mm, "end": v(-1.83, 609.64) * mm});
            skLineSegment(sketch, "E285.11", {"start": v(-1.83, 609.64) * mm, "end": v(-8.06, 586.53) * mm});
            skLineSegment(sketch, "E285.12", {"start": v(-8.06, 586.53) * mm, "end": v(-14.87, 561.3) * mm});
            skLineSegment(sketch, "E285.13", {"start": v(-14.87, 561.3) * mm, "end": v(-22.34, 533.57) * mm});
            skCircle(sketch, "E285.14", {"center": v(23.31, 514.04) * mm, "radius": 3 * mm});
            skCircle(sketch, "E285.15", {"center": v(23.31, 514.04) * mm, "radius": 8.15 * mm});
            skCircle(sketch, "E285.16", {"center": v(16.76, 535.04) * mm, "radius": 3 * mm});
            skCircle(sketch, "E285.17", {"center": v(16.76, 535.04) * mm, "radius": 8.15 * mm});
            skLineSegment(sketch, "E285.18", {"start": v(16.76, 535.04) * mm, "end": v(23.31, 514.04) * mm});
            skLineSegment(sketch, "E285.19", {"start": v(-25.07, 433.87) * mm, "end": v(-23.47, 511.57) * mm});
            skLineSegment(sketch, "E285.20", {"start": v(25.48, 413.86) * mm, "end": v(24.04, 483.94) * mm});
            skLineSegment(sketch, "E285.21", {"start": v(-31.86, 529.57) * mm, "end": v(0.84, 650.86) * mm});
            skLineSegment(sketch, "E285.22", {"start": v(-23.47, 511.57) * mm, "end": v(-23.34, 518.07) * mm});
            skArc(sketch, "E285.23", {"start": v(-23.34, 518.07) * mm, "mid": v(-25.63, 525.28) * mm, "end": v(-31.86, 529.57) * mm});
            skLineSegment(sketch, "E285.24", {"start": v(24.04, 483.94) * mm, "end": v(23.83, 493.94) * mm});
            skLineSegment(sketch, "E285.25", {"start": v(32.65, 511.48) * mm, "end": v(19.25, 554.4) * mm});
            skArc(sketch, "E285.26", {"start": v(23.83, 493.94) * mm, "mid": v(26.06, 503.8) * mm, "end": v(32.65, 511.48) * mm});
            skArc(sketch, "E285.27", {"start": v(0.84, 650.86) * mm, "mid": v(5.02, 641.55) * mm, "end": v(12.58, 634.68) * mm});
            skLineSegment(sketch, "E285.28", {"start": v(-23.47, 511.57) * mm, "end": v(1.17, 511.57) * mm});
            skLineSegment(sketch, "E285.29", {"start": v(3.9, 630.88) * mm, "end": v(-3.97, 633) * mm});
            skArc(sketch, "E285.30", {"start": v(12.58, 634.68) * mm, "mid": v(11.5, 594.18) * mm, "end": v(19.25, 554.4) * mm});
            skLineSegment(sketch, "E285.31", {"start": v(32.65, 511.48) * mm, "end": v(19.25, 554.4) * mm});
            skPoint(sketch, "E286", {"position": v(0, 0) * mm});
            skLineSegment(sketch, "E287", {"start": v(30.78, 0) * mm, "end": v(31.62, -41.26) * mm});
            skLineSegment(sketch, "E288", {"start": v(-30.61, -20.13) * mm, "end": v(-31.54, -65.54) * mm});
            skLineSegment(sketch, "E289", {"start": v(-32.46, -110.96) * mm, "end": v(-33.39, -156.37) * mm});
            skLineSegment(sketch, "E290", {"start": v(32.46, -82.53) * mm, "end": v(33.3, -123.8) * mm});
            skLineSegment(sketch, "E291", {"start": v(33.3, -123.8) * mm, "end": v(34.14, -165.06) * mm});
            skLineSegment(sketch, "E292", {"start": v(-33.39, -156.37) * mm, "end": v(-34.2, -196.66) * mm});
            skLineSegment(sketch, "E293", {"start": v(-31.54, -65.54) * mm, "end": v(-32.46, -110.96) * mm});
            skLineSegment(sketch, "E294", {"start": v(31.62, -41.26) * mm, "end": v(32.46, -82.53) * mm});
            skLineSegment(sketch, "E295", {"start": v(-32.46, -110.96) * mm, "end": v(32.46, -82.53) * mm, "construction": true});
            skLineSegment(sketch, "E296", {"start": v(31.62, -41.26) * mm, "end": v(-31.54, -65.54) * mm, "construction": true});
            skLineSegment(sketch, "E297", {"start": v(-33.39, -156.37) * mm, "end": v(33.3, -123.8) * mm, "construction": true});
            skLineSegment(sketch, "E298", {"start": v(-34.31, -201.78) * mm, "end": v(34.88, -201.78) * mm, "construction": true});
            skLineSegment(sketch, "E299", {"start": v(-0.05, -140.08) * mm, "end": v(-8.14, -123.5) * mm, "construction": true});
            skLineSegment(sketch, "E300", {"start": v(-32.96, -135.63) * mm, "end": v(32.88, -103.46) * mm, "construction": true});
            skLineSegment(sketch, "E301", {"start": v(-0.05, -140.08) * mm, "end": v(-0.05, -119.55) * mm});
            skLineSegment(sketch, "E302", {"start": v(-34.2, -196.66) * mm, "end": v(-34.31, -201.78) * mm});
            skPoint(sketch, "E303", {"position": v(-24, 485.77) * mm});
            skPoint(sketch, "E304", {"position": v(-30.67, 161.93) * mm});
            skLineSegment(sketch, "E305", {"start": v(-30.35, 177.13) * mm, "end": v(-31.2, 136.1) * mm});
            skLineSegment(sketch, "E306", {"start": v(30.27, 181.4) * mm, "end": v(31.03, 144.16) * mm});
            skPoint(sketch, "E307", {"position": v(20.89, 485.77) * mm});
            skPoint(sketch, "E308", {"position": v(24, 485.77) * mm});
            skPoint(sketch, "E309", {"position": v(30.67, 161.93) * mm});
            skLineSegment(sketch, "E310", {"start": v(-33.22, 38) * mm, "end": v(-35.35, -65.54) * mm});
            skLineSegment(sketch, "E311", {"start": v(32.87, 55.04) * mm, "end": v(35.35, -65.54) * mm});
            skLineSegment(sketch, "E312", {"start": v(-34.85, -41.26) * mm, "end": v(34.85, -41.26) * mm});
            skSolve(sketch);
        }
        {
            var Q0;
            Q0=qCreatedBy(makeId("Front.planeOp"),FACE);
            var Q1;
            Q1=sQuery(id+"F8.wireOp",VERTEX,"E307");
            cPlane(context, id + "F9", {"entities" : qUnion([Q0, Q1]), "cplaneType" : CPlaneType.PLANE_POINT, "offset" : 25 * mm, "width" : 150 * mm, "height" : 150 * mm});
        }
        {
            var Q0;
            Q0=qCreatedBy(makeId("Front.planeOp"),FACE);
            var Q1;
            Q1=sQuery(id+"F8.wireOp",VERTEX,"E284.61");
            cPlane(context, id + "F10", {"entities" : qUnion([Q0, Q1]), "cplaneType" : CPlaneType.PLANE_POINT, "offset" : 25 * mm, "width" : 150 * mm, "height" : 150 * mm});
        }
        {
            var Q0;
            Q0=qCreatedBy(makeId("Front.planeOp"),FACE);
            var Q1;
            Q1=sQuery(id+"F8.wireOp",VERTEX,"E296.start");
            cPlane(context, id + "F11", {"entities" : qUnion([Q0, Q1]), "cplaneType" : CPlaneType.PLANE_POINT, "offset" : 25 * mm, "width" : 150 * mm, "height" : 150 * mm});
        }
        {
            var Q0;
            Q0=qCreatedBy(id+"F9.planeOp",FACE);
            var sketch = newSketch(context, id + "F12", { "sketchPlane" : qUnion([Q0])});
            skPoint(sketch, "E313", {"position": v(-24, 0) * mm});
            skArc(sketch, "E314", {"start": v(24, 0) * mm, "mid": v(0, 0.67) * mm, "end": v(-24, 0) * mm});
            skLineSegment(sketch, "E315", {"start": v(0, 0.67) * mm, "end": v(0, -18.33) * mm, "construction": true});
            skLineSegment(sketch, "E316", {"start": v(-24, 0) * mm, "end": v(-24, -3) * mm});
            skLineSegment(sketch, "E317.MirrorCS", {"start": v(24, 0) * mm, "end": v(24, -3) * mm});
            skFitSpline(sketch, "E318", {"points": [v(0, -18.33) * mm, v(-24, -3) * mm], "startDerivative": vector(-24.33, 0) * mm, "endDerivative": vector(0, 26.2) * mm});
            skFitSpline(sketch, "E319.MirrorCS", {"points": [v(0, -18.33) * mm, v(24, -3) * mm], "startDerivative": vector(24.33, 0) * mm, "endDerivative": vector(0, 26.2) * mm});
            skLineSegment(sketch, "E320", {"start": v(24, -3) * mm, "end": v(-24, -3) * mm, "construction": true});
            skSolve(sketch);
        }
        {
            var Q0;
            Q0=qCreatedBy(id+"F10.planeOp",FACE);
            var sketch = newSketch(context, id + "F13", { "sketchPlane" : qUnion([Q0])});
            skArc(sketch, "E321", {"start": v(30.67, 0) * mm, "mid": v(0, 1.1) * mm, "end": v(-30.67, 0) * mm});
            skLineSegment(sketch, "E322", {"start": v(-30.67, 0) * mm, "end": v(-30.67, -3) * mm});
            skLineSegment(sketch, "E323", {"start": v(0, -19.9) * mm, "end": v(0, 1.1) * mm, "construction": true});
            skLineSegment(sketch, "E324.MirrorCS", {"start": v(30.67, 0) * mm, "end": v(30.67, -3) * mm});
            skFitSpline(sketch, "E325", {"points": [v(0, -19.9) * mm, v(-30.67, -3) * mm], "startDerivative": vector(-44.51, 0) * mm, "endDerivative": vector(0, 24.86) * mm});
            skFitSpline(sketch, "E326.MirrorCS", {"points": [v(0, -19.9) * mm, v(30.67, -3) * mm], "startDerivative": vector(44.51, 0) * mm, "endDerivative": vector(0, 24.86) * mm});
            skSolve(sketch);
        }
        {
            var Q0;
            Q0=qCreatedBy(makeId("Right.planeOp"),FACE);
            var sketch = newSketch(context, id + "F14", { "sketchPlane" : qUnion([Q0])});
            skLineSegment(sketch, "E327", {"start": v(658.14, 0.44) * mm, "end": v(-268.77, 1.66) * mm});
            skLineSegment(sketch, "E328", {"start": v(658.14, -17.5) * mm, "end": v(-268.77, -22) * mm});
            skSolve(sketch);
        }
        {
            var Q0;
            Q0=qCreatedBy(id+"F11.planeOp",FACE);
            var sketch = newSketch(context, id + "F15", { "sketchPlane" : qUnion([Q0])});
            skArc(sketch, "E329", {"start": v(34.85, 0) * mm, "mid": v(0, 1.41) * mm, "end": v(-34.85, 0) * mm});
            skLineSegment(sketch, "E330", {"start": v(0, 1.41) * mm, "end": v(0, -20.9) * mm, "construction": true});
            skLineSegment(sketch, "E331", {"start": v(-34.85, 0) * mm, "end": v(-34.85, -3) * mm});
            skFitSpline(sketch, "E332", {"points": [v(0, -20.9) * mm, v(-34.85, -3) * mm], "startDerivative": vector(-55.18, 0) * mm, "endDerivative": vector(0, 24.3) * mm});
            skFitSpline(sketch, "E333.MirrorCS", {"points": [v(0, -20.9) * mm, v(34.85, -3) * mm], "startDerivative": vector(55.18, 0) * mm, "endDerivative": vector(0, 24.3) * mm});
            skLineSegment(sketch, "E334.MirrorCS", {"start": v(34.85, 0) * mm, "end": v(34.85, -3) * mm});
            skSolve(sketch);
        }
        {
            var Q0;
            Q0=makeQuery(id+"F12.imprint","IMPRINT",FACE,{"disambiguationData":[TD([[makeQuery(id+"F12.imprint","IMPRINT",EDGE,{"derivedFrom":sQuery(id+"F12.wireOp",EDGE,"E314")}),1.0]])]});
            var Q1;
            Q1=makeQuery(id+"F15.imprint","IMPRINT",FACE,{"disambiguationData":[TD([[makeQuery(id+"F15.imprint","IMPRINT",EDGE,{"derivedFrom":sQuery(id+"F15.wireOp",EDGE,"E329")}),1.0]])]});
            loft(context, id + "F16", {"sheetProfilesArray" : [{ "sheetProfileEntities" : qUnion([Q0]) }, { "sheetProfileEntities" : qUnion([Q1]) }]});
        }
        {
            var Q0;
            Q0=qCreatedBy(id+"F9.planeOp",FACE);
            var sketch = newSketch(context, id + "F17", { "sketchPlane" : qUnion([Q0])});
            skLineSegment(sketch, "E335.bottom", {"start": v(-31.86, 0) * mm, "end": v(32.65, 0) * mm});
            skLineSegment(sketch, "E335.top", {"start": v(-31.86, -35) * mm, "end": v(32.65, -35) * mm});
            skLineSegment(sketch, "E335.left", {"start": v(-31.86, 0) * mm, "end": v(-31.86, -35) * mm});
            skLineSegment(sketch, "E335.right", {"start": v(32.65, 0) * mm, "end": v(32.65, -35) * mm});
            skSolve(sketch);
        }
        {
            var Q0;
            Q0 = qSketchRegion(id + "F17", true);
            var Q1;
            Q1=sQuery(id+"F8.wireOp",VERTEX,"E285.21.end");
            extrude(context, id + "F18", {"entities" : qUnion([Q0]), "operationType" : NewBodyOperationType.ADD, "endBound" : BoundingType.UP_TO_VERTEX, "oppositeDirection" : true, "endBoundEntityVertex" : qUnion([Q1]), "depth" : 25 * mm});
        }
        {
            var Q0;
            Q0=sQuery(id+"F8.wireOp",EDGE,"E284.0");
            cPlane(context, id + "F19", {"entities" : qUnion([Q0]), "cplaneType" : CPlaneType.MID_PLANE, "offset" : 25 * mm, "width" : 150 * mm, "height" : 150 * mm});
        }
        {
            var Q0;
            Q0=qCreatedBy(id+"F19.planeOp",FACE);
            var sketch = newSketch(context, id + "F20", { "sketchPlane" : qUnion([Q0])});
            skLineSegment(sketch, "E336", {"start": v(-430.41, 0) * mm, "end": v(-603.46, -22.78) * mm});
            skLineSegment(sketch, "E337", {"start": v(-603.46, 0) * mm, "end": v(-430.41, 0) * mm, "construction": true});
            skLineSegment(sketch, "E338", {"start": v(-603.46, -22.78) * mm, "end": v(-603.46, 11.43) * mm});
            skLineSegment(sketch, "E339", {"start": v(-603.46, 11.43) * mm, "end": v(-430.41, 11.43) * mm});
            skLineSegment(sketch, "E340", {"start": v(-430.41, 11.43) * mm, "end": v(-430.41, 0) * mm});
            skLineSegment(sketch, "E341", {"start": v(-579.03, -19.57) * mm, "end": v(-577.46, -31.46) * mm});
            skLineSegment(sketch, "E342", {"start": v(-577.46, -31.46) * mm, "end": v(-430.41, -12.1) * mm});
            skLineSegment(sketch, "E343", {"start": v(-430.41, -12.1) * mm, "end": v(-430.41, 0) * mm, "construction": true});
            skLineSegment(sketch, "E344", {"start": v(-603.46, -22.78) * mm, "end": v(-603.46, -42.48) * mm});
            skLineSegment(sketch, "E345", {"start": v(-603.46, -42.48) * mm, "end": v(-430.41, -42.48) * mm});
            skLineSegment(sketch, "E346", {"start": v(-430.41, -42.48) * mm, "end": v(-430.41, -12.1) * mm});
            skSolve(sketch);
        }
        {
            var Q0;
            Q0 = qSketchRegion(id + "F20", true);
            extrude(context, id + "F21", {"entities" : qUnion([Q0]), "operationType" : NewBodyOperationType.REMOVE, "endBound" : BoundingType.THROUGH_ALL, "oppositeDirection" : true, "depth" : 25 * mm, "hasSecondDirection" : true, "secondDirectionBound" : SecondDirectionBoundingType.THROUGH_ALL, "secondDirectionOppositeDirection" : false, "secondDirectionDepth" : 25 * mm});
        }
        {
            var Q0;
            Q0=qCreatedBy(makeId("Top.planeOp"),FACE);
            var sketch = newSketch(context, id + "F22", { "sketchPlane" : qUnion([Q0])});
            skLineSegment(sketch, "E347.0", {"start": v(-23.47, 511.57) * mm, "end": v(-23.34, 518.07) * mm});
            skArc(sketch, "E347.1", {"start": v(-23.34, 518.07) * mm, "mid": v(-25.63, 525.28) * mm, "end": v(-31.86, 529.57) * mm});
            skLineSegment(sketch, "E347.2", {"start": v(-31.86, 529.57) * mm, "end": v(0.84, 650.86) * mm});
            skArc(sketch, "E347.3", {"start": v(0.84, 650.86) * mm, "mid": v(5.02, 641.55) * mm, "end": v(12.58, 634.68) * mm});
            skArc(sketch, "E347.4", {"start": v(12.58, 634.68) * mm, "mid": v(11.5, 594.18) * mm, "end": v(19.25, 554.4) * mm});
            skLineSegment(sketch, "E347.5", {"start": v(32.65, 511.48) * mm, "end": v(19.25, 554.4) * mm});
            skArc(sketch, "E347.6", {"start": v(23.83, 493.94) * mm, "mid": v(26.06, 503.8) * mm, "end": v(32.65, 511.48) * mm});
            skLineSegment(sketch, "E347.7", {"start": v(24.04, 483.94) * mm, "end": v(23.83, 493.94) * mm});
            skLineSegment(sketch, "E348", {"start": v(-23.47, 511.57) * mm, "end": v(-24, 485.77) * mm});
            skLineSegment(sketch, "E349", {"start": v(-24, 485.77) * mm, "end": v(-50.4, 480.01) * mm});
            skLineSegment(sketch, "E350", {"start": v(-50.4, 480.01) * mm, "end": v(-50.4, 656.25) * mm});
            skLineSegment(sketch, "E351", {"start": v(-50.4, 656.25) * mm, "end": v(47.94, 656.25) * mm});
            skLineSegment(sketch, "E352", {"start": v(47.94, 656.25) * mm, "end": v(47.94, 474.65) * mm});
            skLineSegment(sketch, "E353", {"start": v(47.94, 474.65) * mm, "end": v(24.04, 483.94) * mm});
            skSolve(sketch);
        }
        {
            var Q0;
            Q0 = qSketchRegion(id + "F22", true);
            extrude(context, id + "F23", {"entities" : qUnion([Q0]), "operationType" : NewBodyOperationType.REMOVE, "endBound" : BoundingType.THROUGH_ALL, "oppositeDirection" : true, "depth" : 25 * mm});
        }
    });
